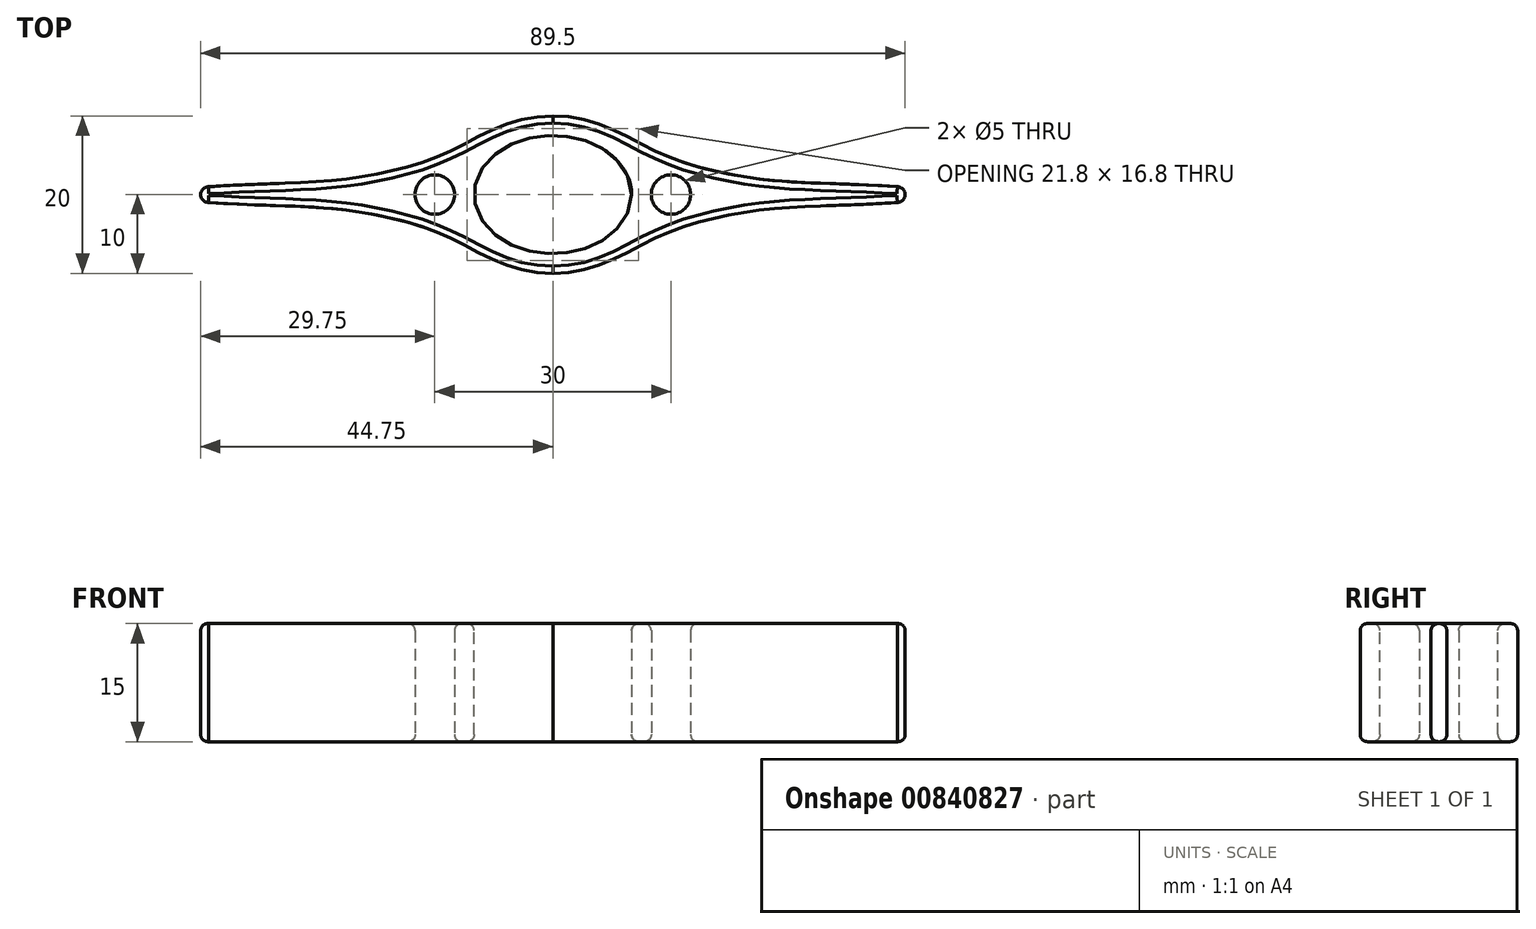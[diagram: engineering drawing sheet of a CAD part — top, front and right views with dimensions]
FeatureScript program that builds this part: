
annotation { "Feature Type Name" : "Feature", "Feature Type Description" : "" }
export const myFeature = defineFeature(function(context is Context, id is Id, definition is map)
    precondition{}
    {
        {
            var Q0;
            Q0=qCreatedBy(makeId("Top.planeOp"),FACE);
            var sketch = newSketch(context, id + "F0", { "sketchPlane" : qUnion([Q0])});
            skLineSegment(sketch, "E0", {"start": v(-43.75, 0) * mm, "end": v(43.75, 0) * mm, "construction": true});
            skArc(sketch, "E1", {"start": v(-43.75, 1) * mm, "mid": v(-44.75, 0) * mm, "end": v(-43.75, -1) * mm});
            skEllipse(sketch, "E2", {"center": v(0, 0) * mm, "majorRadius": 10 * mm, "minorRadius": 7.5 * mm, "majorAxis": v(1, 0)});
            skLineSegment(sketch, "E3", {"start": v(0, 43.75) * mm, "end": v(0, -43.75) * mm, "construction": true});
            skFitSpline(sketch, "E4", {"points": [v(-43.75, 1) * mm, v(-27.76, 1.81) * mm, v(-13.67, 5.22) * mm, v(0, 10) * mm], "startDerivative": vector(67.13, 4.39) * mm, "endDerivative": vector(55.01, 0.28) * mm});
            skFitSpline(sketch, "E5.MirrorCS", {"points": [v(-43.75, -1) * mm, v(-27.76, -1.81) * mm, v(-13.67, -5.22) * mm, v(0, -10) * mm], "startDerivative": vector(67.13, -4.39) * mm, "endDerivative": vector(55.01, -0.28) * mm});
            skFitSpline(sketch, "E6.MirrorCS", {"points": [v(43.75, 1) * mm, v(27.76, 1.81) * mm, v(13.67, 5.22) * mm, v(0, 10) * mm], "startDerivative": vector(-67.13, 4.39) * mm, "endDerivative": vector(-55.01, 0.28) * mm});
            skArc(sketch, "E7.MirrorCS", {"start": v(43.75, 1) * mm, "mid": v(44.75, 0) * mm, "end": v(43.75, -1) * mm});
            skFitSpline(sketch, "E8.MirrorCS", {"points": [v(43.75, -1) * mm, v(27.76, -1.81) * mm, v(13.67, -5.22) * mm, v(0, -10) * mm], "startDerivative": vector(-67.13, -4.39) * mm, "endDerivative": vector(-55.01, -0.28) * mm});
            skCircle(sketch, "E9", {"center": v(-15, 0) * mm, "radius": 2.5 * mm});
            skCircle(sketch, "E10.MirrorC", {"center": v(15, 0) * mm, "radius": 2.5 * mm});
            skSolve(sketch);
        }
        {
            var Q0;
            Q0=makeQuery(id+"F0.imprint","IMPRINT",FACE,{"disambiguationData":[TD([[makeQuery(id+"F0.imprint","IMPRINT",EDGE,{"derivedFrom":sQuery(id+"F0.wireOp",EDGE,"E1")}),1.0]])]});
            extrude(context, id + "F1", {"entities" : qUnion([Q0]), "depth" : 15 * mm, "offsetDistance" : 25 * mm});
        }
        {
            var Q0;
            Q0=makeQuery(id+"F1.opExtrude","CAP_FACE",FACE,{"disambiguationData":[OSD([sQuery(id+"F0.wireOp",EDGE,"E1"),sQuery(id+"F0.wireOp",EDGE,"E2"),sQuery(id+"F0.wireOp",EDGE,"E4"),sQuery(id+"F0.wireOp",EDGE,"E5.MirrorCS"),sQuery(id+"F0.wireOp",EDGE,"E6.MirrorCS"),sQuery(id+"F0.wireOp",EDGE,"E7.MirrorCS"),sQuery(id+"F0.wireOp",EDGE,"E8.MirrorCS")])],"isStart":false});
            var Q1;
            Q1=makeQuery(id+"F1.opExtrude","CAP_FACE",FACE,{"disambiguationData":[OSD([sQuery(id+"F0.wireOp",EDGE,"E1"),sQuery(id+"F0.wireOp",EDGE,"E2"),sQuery(id+"F0.wireOp",EDGE,"E4"),sQuery(id+"F0.wireOp",EDGE,"E5.MirrorCS"),sQuery(id+"F0.wireOp",EDGE,"E6.MirrorCS"),sQuery(id+"F0.wireOp",EDGE,"E7.MirrorCS"),sQuery(id+"F0.wireOp",EDGE,"E8.MirrorCS")])],"isStart":true});
            fillet(context, id + "F2", {"entities" : qUnion([Q0, Q1]), "radius" : 0.9 * mm, "tangentPropagation" : true, "allowEdgeOverflow" : false});
        }
    });
